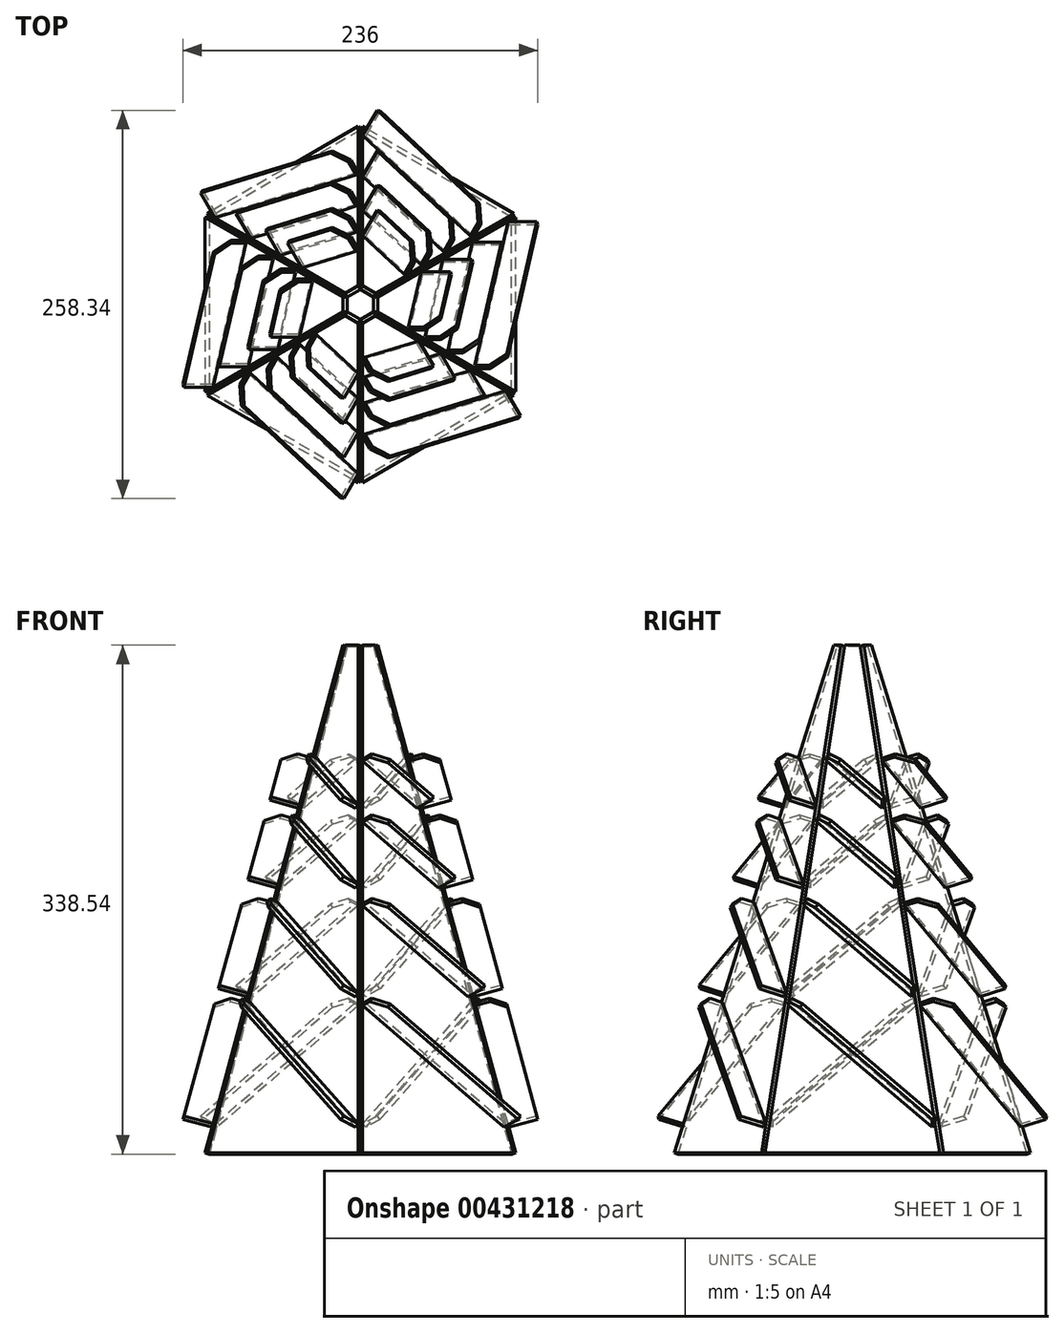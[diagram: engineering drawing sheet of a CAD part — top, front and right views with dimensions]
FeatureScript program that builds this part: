
annotation { "Feature Type Name" : "Feature", "Feature Type Description" : "" }
export const myFeature = defineFeature(function(context is Context, id is Id, definition is map)
    precondition{}
    {
        {
            var Q0;
            Q0=qCreatedBy(makeId("Top.planeOp"),FACE);
            var sketch = newSketch(context, id + "F0", { "sketchPlane" : qUnion([Q0])});
            skCircle(sketch, "E0.cCircle", {"center": v(0, 0) * mm, "radius": 100.46 * mm, "construction": true});
            skLineSegment(sketch, "E0.0", {"start": v(-100.46, -58) * mm, "end": v(-100.46, 58) * mm, "construction": true});
            skLineSegment(sketch, "E0.1", {"start": v(-100.46, 58) * mm, "end": v(0, 116) * mm, "construction": true});
            skLineSegment(sketch, "E0.2", {"start": v(0, 116) * mm, "end": v(100.46, 58) * mm, "construction": true});
            skLineSegment(sketch, "E0.3", {"start": v(100.46, 58) * mm, "end": v(100.46, -58) * mm, "construction": true});
            skLineSegment(sketch, "E0.4", {"start": v(100.46, -58) * mm, "end": v(0, -116) * mm, "construction": true});
            skLineSegment(sketch, "E0.5", {"start": v(0, -116) * mm, "end": v(-100.46, -58) * mm, "construction": true});
            skPoint(sketch, "E0.0.midPoint", {"position": v(-100.46, 0) * mm});
            skLineSegment(sketch, "E1", {"start": v(0, 116) * mm, "end": v(100.46, 58) * mm});
            skLineSegment(sketch, "E2", {"start": v(100.46, 58) * mm, "end": v(101.96, 60.6) * mm});
            skLineSegment(sketch, "E3", {"start": v(101.96, 60.6) * mm, "end": v(1.5, 118.6) * mm});
            skLineSegment(sketch, "E4", {"start": v(1.5, 118.6) * mm, "end": v(0, 116) * mm});
            skSolve(sketch);
        }
        {
            var Q0;
            Q0=qCreatedBy(makeId("Right.planeOp"),FACE);
            var sketch = newSketch(context, id + "F1", { "sketchPlane" : qUnion([Q0])});
            skLineSegment(sketch, "E5", {"start": v(0, 39.63) * mm, "end": v(116, 39.63) * mm});
            skLineSegment(sketch, "E6", {"start": v(116, 39.63) * mm, "end": v(63, 389.63) * mm});
            skLineSegment(sketch, "E7", {"start": v(63, 389.63) * mm, "end": v(53, 389.63) * mm});
            skLineSegment(sketch, "E8", {"start": v(53, 389.63) * mm, "end": v(0, 39.63) * mm});
            skPoint(sketch, "E9", {"position": v(58, 389.63) * mm});
            skPoint(sketch, "E10", {"position": v(58, 39.63) * mm});
            skLineSegment(sketch, "E11", {"start": v(0, 0) * mm, "end": v(0, 31.85) * mm, "construction": true});
            skSolve(sketch);
        }
        {
            var Q0;
            Q0 = qSketchRegion(id + "F1", true);
            extrude(context, id + "F2", {"entities" : qUnion([Q0]), "depth" : 3 * mm});
        }
        {
            var Q0;
            Q0=makeQuery(id+"F2.opExtrude","CAP_FACE",FACE,{"disambiguationData":[OSD([sQuery(id+"F1.wireOp",EDGE,"E5"),sQuery(id+"F1.wireOp",EDGE,"E6"),sQuery(id+"F1.wireOp",EDGE,"E7"),sQuery(id+"F1.wireOp",EDGE,"E8")])],"isStart":false});
            var sketch = newSketch(context, id + "F3", { "sketchPlane" : qUnion([Q0])});
            skLineSegment(sketch, "E12", {"start": v(40.89, 309.63) * mm, "end": v(42.86, 311.88) * mm});
            skLineSegment(sketch, "E13", {"start": v(42.86, 311.88) * mm, "end": v(79.66, 279.63) * mm});
            skLineSegment(sketch, "E14", {"start": v(79.66, 279.63) * mm, "end": v(77.68, 277.37) * mm});
            skLineSegment(sketch, "E15", {"start": v(77.68, 277.37) * mm, "end": v(40.89, 309.63) * mm});
            skLineSegment(sketch, "E16", {"start": v(34.5, 267.52) * mm, "end": v(86, 222.37) * mm});
            skLineSegment(sketch, "E17", {"start": v(86, 222.37) * mm, "end": v(87.99, 224.63) * mm});
            skLineSegment(sketch, "E18", {"start": v(87.99, 224.63) * mm, "end": v(36.49, 269.78) * mm});
            skLineSegment(sketch, "E19", {"start": v(36.49, 269.78) * mm, "end": v(34.5, 267.52) * mm});
            skLineSegment(sketch, "E20", {"start": v(25.81, 210.1) * mm, "end": v(97.37, 147.37) * mm});
            skLineSegment(sketch, "E21", {"start": v(97.37, 147.37) * mm, "end": v(99.34, 149.63) * mm});
            skLineSegment(sketch, "E22", {"start": v(99.34, 149.63) * mm, "end": v(27.8, 212.35) * mm});
            skLineSegment(sketch, "E23", {"start": v(27.8, 212.35) * mm, "end": v(25.81, 210.1) * mm});
            skLineSegment(sketch, "E24", {"start": v(15.38, 141.2) * mm, "end": v(111, 57.37) * mm});
            skLineSegment(sketch, "E25", {"start": v(111, 57.37) * mm, "end": v(112.97, 59.63) * mm});
            skLineSegment(sketch, "E26", {"start": v(112.97, 59.63) * mm, "end": v(17.36, 143.45) * mm});
            skLineSegment(sketch, "E27", {"start": v(17.36, 143.45) * mm, "end": v(15.38, 141.2) * mm});
            skSolve(sketch);
        }
        {
            var Q0;
            Q0 = qSketchRegion(id + "F3", true);
            extrude(context, id + "F4", {"entities" : qUnion([Q0]), "operationType" : NewBodyOperationType.ADD, "depth" : 20 * mm});
        }
        {
            var Q0;
            Q0=makeQuery(id+"F4.opExtrude","CAP_EDGE",EDGE,{"disambiguationData":[OSD([sQuery(id+"F3.wireOp",EDGE,"E12")])],"isStart":false});
            var Q1;
            Q1=makeQuery(id+"F4.opExtrude","CAP_EDGE",EDGE,{"disambiguationData":[OSD([sQuery(id+"F3.wireOp",EDGE,"E19")])],"isStart":false});
            var Q2;
            Q2=makeQuery(id+"F4.opExtrude","CAP_EDGE",EDGE,{"disambiguationData":[OSD([sQuery(id+"F3.wireOp",EDGE,"E23")])],"isStart":false});
            var Q3;
            Q3=makeQuery(id+"F4.opExtrude","CAP_EDGE",EDGE,{"disambiguationData":[OSD([sQuery(id+"F3.wireOp",EDGE,"E27")])],"isStart":false});
            chamfer(context, id + "F5", {"entities" : qUnion([Q0, Q1, Q2, Q3]), "width" : 10 * mm, "tangentPropagation" : true});
        }
        {
            var Q0;
            Q0=makeQuery(id+"F2.opExtrude","SWEPT_BODY",BODY,{"disambiguationData":[OSD([sQuery(id+"F1.wireOp",EDGE,"E5"),sQuery(id+"F1.wireOp",EDGE,"E6"),sQuery(id+"F1.wireOp",EDGE,"E7"),sQuery(id+"F1.wireOp",EDGE,"E8")])]});
            var Q1;
            Q1=sQuery(id+"F0.wireOp",VERTEX,"E0.cCircle.center");
            var Q2;
            Q2=sQuery(id+"F0.wireOp",VERTEX,"E0.4.start");
            transform(context, id + "F6", {"entities" : qUnion([Q0]), "transformType" : TransformType.TRANSLATION_ENTITY, "oppositeDirectionEntity" : false, "transformLine" : qUnion([Q1, Q2]), "makeCopy" : false});
        }
        {
            var Q0;
            Q0=makeQuery(id+"F2.opExtrude","SWEPT_BODY",BODY,{"disambiguationData":[OSD([sQuery(id+"F1.wireOp",EDGE,"E5"),sQuery(id+"F1.wireOp",EDGE,"E6"),sQuery(id+"F1.wireOp",EDGE,"E7"),sQuery(id+"F1.wireOp",EDGE,"E8")])]});
            var Q1;
            Q1=makeQuery(id+"F2.opExtrude","CAP_EDGE",EDGE,{"disambiguationData":[OSD([sQuery(id+"F1.wireOp",EDGE,"E5")])],"isStart":true});
            transform(context, id + "F7", {"entities" : qUnion([Q0]), "transformType" : TransformType.ROTATION, "transformAxis" : qUnion([Q1]), "angle" : 15.2 * degree, "oppositeDirection" : true, "makeCopy" : false});
        }
        {
            var Q0;
            Q0=makeQuery(id+"F2.opExtrude","SWEPT_BODY",BODY,{"disambiguationData":[OSD([sQuery(id+"F1.wireOp",EDGE,"E5"),sQuery(id+"F1.wireOp",EDGE,"E6"),sQuery(id+"F1.wireOp",EDGE,"E7"),sQuery(id+"F1.wireOp",EDGE,"E8")])]});
            var Q1;
            Q1=sQuery(id+"F1.wireOp",EDGE,"E11");
            circularPattern(context, id + "F8", {"entities" : qUnion([Q0]), "axis" : qUnion([Q1]), "angle" : 360 * degree, "instanceCount" : 6, "equalSpace" : true});
        }
    });
